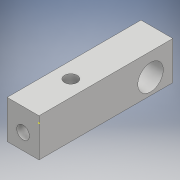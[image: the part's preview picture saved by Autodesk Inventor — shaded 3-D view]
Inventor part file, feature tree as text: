
AUTODESK INVENTOR PART (.ipt)
format: ipt  version: 2017 SP1 (Build 210196100, 196)  size: 249,856 bytes
history: native  units: mm
features: sketch x7, extrude x3, hole x3
ambient origin geometry x8: Origin, YZ Plane, XZ Plane, XY Plane, X Axis, Y Axis, Z Axis, Center Point
bodies: Solide1 (feature_tree)
feature tree (13):
  extrude  "Extrusion1"  Depth=40.0mm
  hole  "Perçage1"  [1 undecoded]
  extrude  "Extrusion2"  Depth=10.0mm TaperAngle=0.0deg
  extrude  "Extrusion3"  Depth=5.0mm
  sketch  "Esquisse5"
  hole  "Perçage2"  [1 undecoded]
  hole  "Perçage3"  [1 undecoded]
  sketch  "Esquisse1"
  sketch  "Esquisse2"
  sketch  "Esquisse3"
  sketch  "Esquisse4"
  sketch  "Esquisse6"
  sketch  "Esquisse7"
note: 3 required parameter values undecoded (feature->parameter linkage not recoverable at this tier; creation-order binding heuristic only, values carry confidence <= 0.55)
